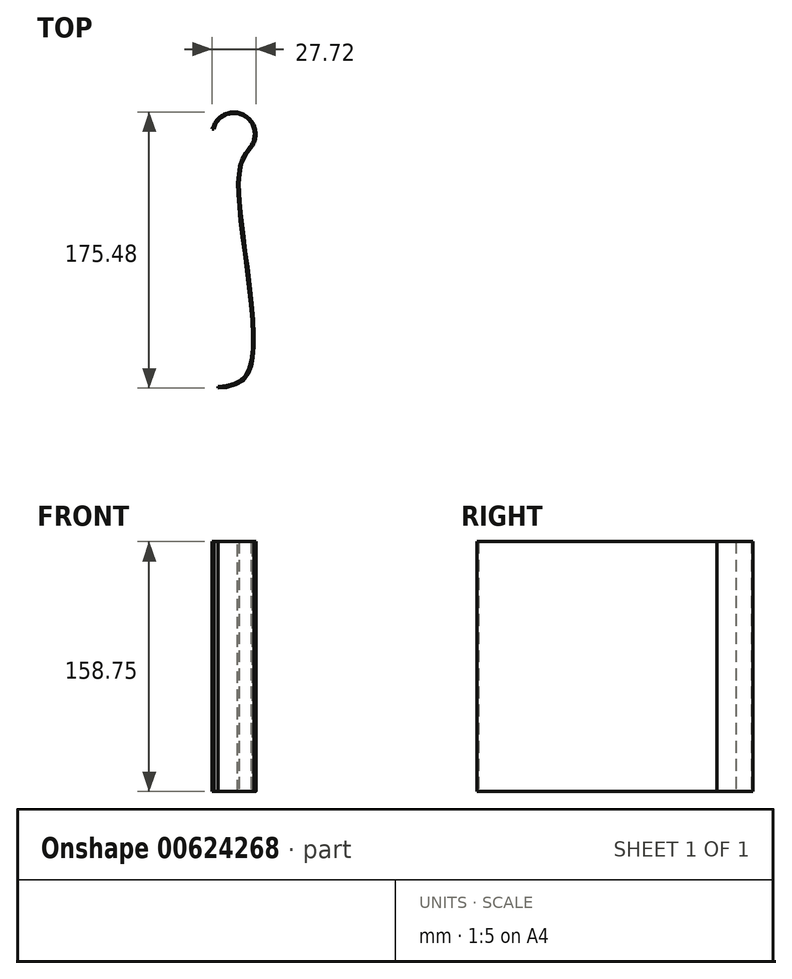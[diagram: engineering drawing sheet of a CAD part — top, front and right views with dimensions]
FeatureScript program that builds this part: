
annotation { "Feature Type Name" : "Feature", "Feature Type Description" : "" }
export const myFeature = defineFeature(function(context is Context, id is Id, definition is map)
    precondition{}
    {
        {
            var Q0;
            Q0=qCreatedBy(makeId("Top.planeOp"),FACE);
            var sketch = newSketch(context, id + "F0", { "sketchPlane" : qUnion([Q0])});
            skPoint(sketch, "E0.4.internal.snap0", {"position": v(7.38, -37.26) * mm});
            skPoint(sketch, "E1", {"position": v(0, 70.32) * mm});
            skFitSpline(sketch, "E2", {"points": [v(0, -49.96) * mm, v(20.08, -37.26) * mm, v(12.7, 70.32) * mm, v(20.08, 102.19) * mm], "startDerivative": vector(131.84, 12.54) * mm, "endDerivative": vector(70.16, 84.77) * mm});
            skPoint(sketch, "E3.start.orphan", {"position": v(-5.32, -37.26) * mm});
            skArc(sketch, "E4", {"start": v(20.08, 102.19) * mm, "mid": v(15.89, 122.14) * mm, "end": v(-2.62, 113.58) * mm});
            skArc(sketch, "E5.0", {"start": v(20.85, 101.55) * mm, "mid": v(16.23, 123.09) * mm, "end": v(-3.65, 113.58) * mm});
            skFitSpline(sketch, "E5.1", {"points": [v(0.1, -50.96) * mm, v(2.86, -50.7) * mm, v(6.69, -50.2) * mm, v(11.12, -48.88) * mm, v(14.1, -47.45) * mm, v(16.7, -45.44) * mm, v(18.86, -42.77) * mm, v(20.25, -39.96) * mm, v(21.13, -37.31) * mm, v(21.86, -34.4) * mm, v(22.49, -30.27) * mm, v(22.87, -24.64) * mm, v(22.93, -18.41) * mm, v(22.63, -9.43) * mm, v(21.65, 2.83) * mm, v(19.86, 18.46) * mm, v(18.14, 31.6) * mm, v(16.8, 41.81) * mm, v(15.85, 49.21) * mm, v(15, 56.26) * mm, v(14.29, 62.87) * mm, v(13.85, 67.92) * mm, v(13.62, 71.64) * mm, v(13.46, 75.13) * mm, v(13.42, 79.12) * mm, v(13.63, 83.35) * mm, v(14.1, 87.1) * mm, v(15.1, 91.58) * mm, v(17.03, 96.38) * mm, v(19.42, 99.82) * mm, v(20.85, 101.55) * mm]});
            skLineSegment(sketch, "E6", {"start": v(-3.65, 113.58) * mm, "end": v(-2.62, 113.58) * mm});
            skPoint(sketch, "E7.orphan", {"position": v(0, 102.19) * mm});
            skLineSegment(sketch, "E8", {"start": v(0, -49.96) * mm, "end": v(0.1, -50.96) * mm});
            skSolve(sketch);
        }
        {
            var Q0;
            Q0=qSketchRegion(id+"F0",true);
            extrude(context, id + "F1", {"entities" : qUnion([Q0]), "depth" : 158.75 * mm, "offsetDistance" : 25.4 * mm});
        }
    });
